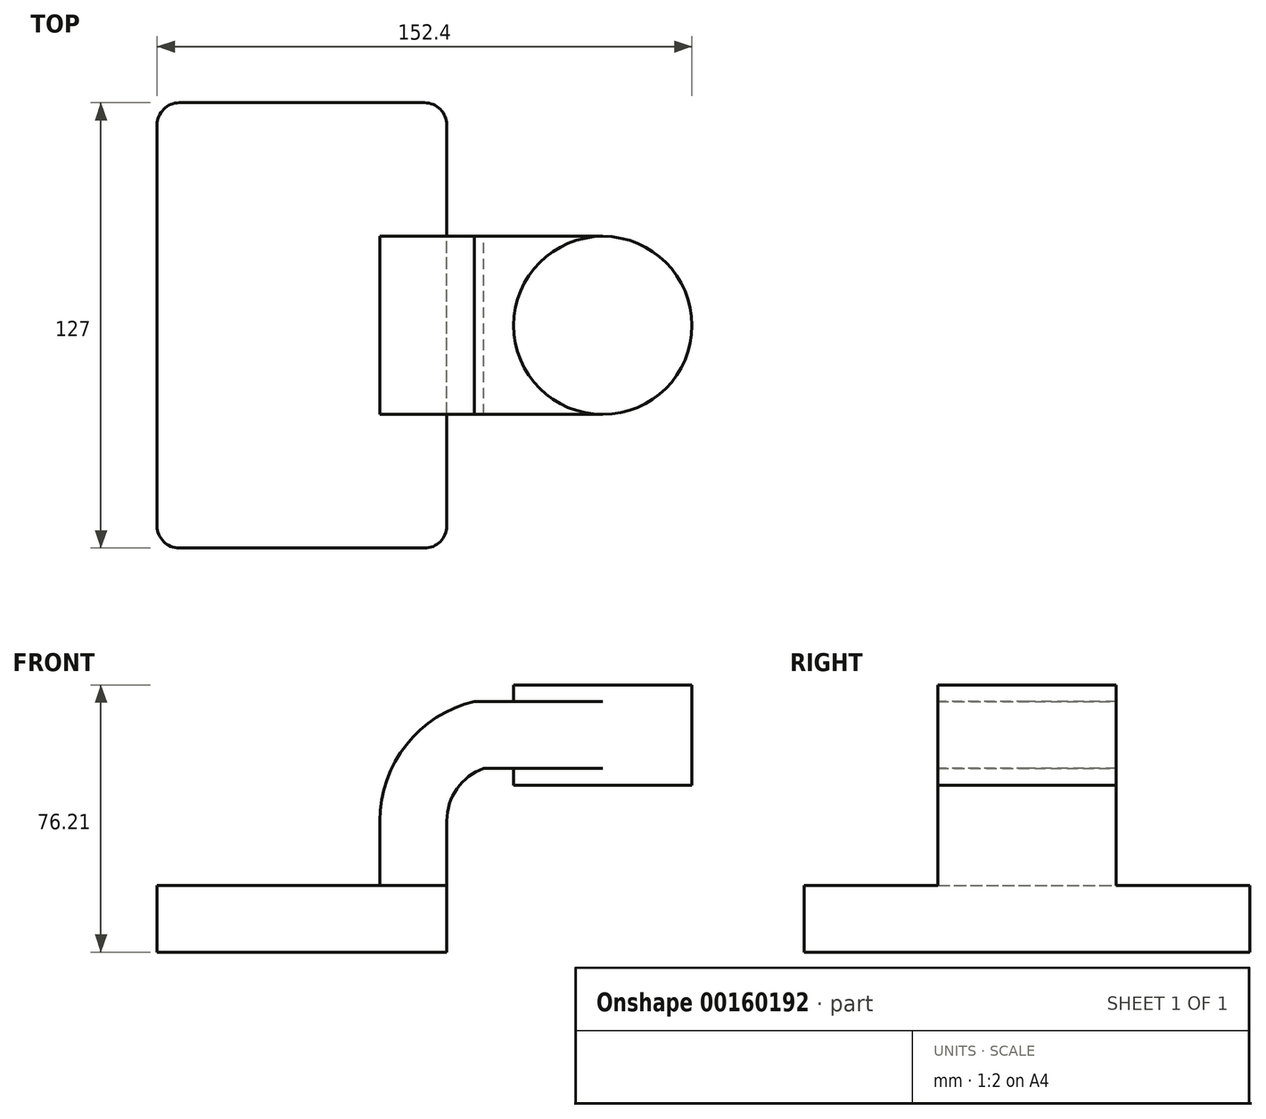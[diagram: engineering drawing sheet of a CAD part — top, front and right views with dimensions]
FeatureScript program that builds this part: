
annotation { "Feature Type Name" : "Feature", "Feature Type Description" : "" }
export const myFeature = defineFeature(function(context is Context, id is Id, definition is map)
    precondition{}
    {
        {
            var Q0;
            Q0=qCreatedBy(makeId("Front.planeOp"),FACE);
            var sketch = newSketch(context, id + "F0", { "sketchPlane" : qUnion([Q0])});
            skLineSegment(sketch, "E0.bottom", {"start": v(-41.28, 9.52) * mm, "end": v(41.28, 9.53) * mm});
            skLineSegment(sketch, "E0.top", {"start": v(-41.28, -9.53) * mm, "end": v(41.28, -9.53) * mm});
            skLineSegment(sketch, "E0.left", {"start": v(-41.28, 9.52) * mm, "end": v(-41.27, -9.53) * mm});
            skLineSegment(sketch, "E0.right", {"start": v(41.27, 9.53) * mm, "end": v(41.28, -9.52) * mm});
            skPoint(sketch, "E0.middle", {"position": v(0, 0) * mm});
            skLineSegment(sketch, "E1.bottom", {"start": v(111.12, 38.1) * mm, "end": v(60.32, 38.1) * mm});
            skLineSegment(sketch, "E1.top", {"start": v(111.12, 66.68) * mm, "end": v(60.32, 66.68) * mm});
            skLineSegment(sketch, "E1.left", {"start": v(111.12, 38.1) * mm, "end": v(111.12, 66.68) * mm});
            skLineSegment(sketch, "E1.right", {"start": v(60.32, 38.1) * mm, "end": v(60.32, 66.68) * mm});
            skPoint(sketch, "E1.middle", {"position": v(85.72, 52.39) * mm});
            skLineSegment(sketch, "E2", {"start": v(41.27, 9.52) * mm, "end": v(41.27, 27.94) * mm});
            skArc(sketch, "E3", {"start": v(41.28, 27.94) * mm, "mid": v(44.16, 37.07) * mm, "end": v(51.77, 42.88) * mm});
            skLineSegment(sketch, "E4", {"start": v(51.77, 42.88) * mm, "end": v(107.14, 42.88) * mm});
            skLineSegment(sketch, "E5.0", {"start": v(49.1, 61.93) * mm, "end": v(85.72, 61.93) * mm});
            skArc(sketch, "E5.1", {"start": v(22.23, 27.94) * mm, "mid": v(29.76, 49.6) * mm, "end": v(49.1, 61.93) * mm});
            skLineSegment(sketch, "E5.2", {"start": v(22.22, 9.52) * mm, "end": v(22.22, 27.94) * mm});
            skLineSegment(sketch, "E6", {"start": v(85.72, 38.1) * mm, "end": v(85.72, 61.93) * mm});
            skLineSegment(sketch, "E7", {"start": v(85.72, 61.93) * mm, "end": v(85.72, 66.68) * mm});
            skFitSpline(sketch, "E8", {"points": [v(-41.28, 9.52) * mm, v(49.1, 61.93) * mm], "startDerivative": vector(0.43, 78.43) * mm, "endDerivative": vector(112.9, -3.22) * mm});
            skSolve(sketch);
        }
        {
            var Q0;
            Q0=makeQuery(id+"F0.imprint","IMPRINT",FACE,{"disambiguationData":[TD([[makeQuery(id+"F0.imprint","IMPRINT",EDGE,{"derivedFrom":sQuery(id+"F0.wireOp",EDGE,"E0.top")}),1.0]])]});
            extrude(context, id + "F1", {"entities" : qUnion([Q0]), "endBound" : BoundingType.SYMMETRIC, "depth" : 127 * mm});
        }
        {
            var Q0;
            {var subQ1=sQuery(id+"F0.wireOp",EDGE,"E2");Q0=makeQuery(id+"F0.imprint","IMPRINT",FACE,{"disambiguationData":[TD([[makeQuery(id+"F0.imprint","IMPRINT",EDGE,{"derivedFrom":subQ1}),1.0]])]});}
            var Q1;
            {var subQ0=sQuery(id+"F0.wireOp",EDGE,"E4");var subQ1=sQuery(id+"F0.wireOp",EDGE,"E1.right");var subQ2=makeQuery(id+"F0.imprint","INTERSECT",VERTEX,{"derivedFrom":[subQ1,subQ0]});Q1=makeQuery(id+"F0.imprint","IMPRINT",FACE,{"disambiguationData":[TD([[makeQuery(id+"F0.imprint","IMPRINT",EDGE,{"disambiguationData":[TD([[subQ2,-1.0]])],"derivedFrom":subQ1}),-1.0]])]});}
            extrude(context, id + "F2", {"entities" : qUnion([Q0, Q1]), "operationType" : NewBodyOperationType.ADD, "endBound" : BoundingType.SYMMETRIC, "depth" : 50.8 * mm});
        }
        {
            var Q0;
            Q0=makeQuery(id+"F0.imprint","IMPRINT",FACE,{"disambiguationData":[TD([[makeQuery(id+"F0.imprint","IMPRINT",EDGE,{"derivedFrom":sQuery(id+"F0.wireOp",EDGE,"E5.1")}),1.0]])]});
            extrude(context, id + "F3", {"entities" : qUnion([Q0]), "operationType" : NewBodyOperationType.ADD, "endBound" : BoundingType.SYMMETRIC, "depth" : 15.88 * mm});
        }
        {
            var Q0;
            {var subQ0=sQuery(id+"F0.wireOp",EDGE,"E1.left");Q0=makeQuery(id+"F0.imprint","IMPRINT",FACE,{"disambiguationData":[TD([[makeQuery(id+"F0.imprint","IMPRINT",EDGE,{"derivedFrom":subQ0}),1.0]])]});}
            var Q1;
            Q1=sQuery(id+"F0.wireOp",EDGE,"E6");
            revolve(context, id + "F4", {"operationType" : NewBodyOperationType.ADD, "entities" : qUnion([Q0]), "axis" : qUnion([Q1]), "revolveType" : RevolveType.FULL});
        }
        {
            var Q0;
            Q0=makeQuery(id+"F1.opExtrude","CAP_EDGE",EDGE,{"disambiguationData":[OSD([sQuery(id+"F0.wireOp",EDGE,"E0.right")])],"isStart":false});
            var Q1;
            Q1=makeQuery(id+"F1.opExtrude","CAP_EDGE",EDGE,{"disambiguationData":[OSD([sQuery(id+"F0.wireOp",EDGE,"E0.left")])],"isStart":false});
            var Q2;
            Q2=makeQuery(id+"F1.opExtrude","CAP_EDGE",EDGE,{"disambiguationData":[OSD([sQuery(id+"F0.wireOp",EDGE,"E0.right")])],"isStart":true});
            var Q3;
            Q3=makeQuery(id+"F1.opExtrude","CAP_EDGE",EDGE,{"disambiguationData":[OSD([sQuery(id+"F0.wireOp",EDGE,"E0.left")])],"isStart":true});
            fillet(context, id + "F5", {"entities" : qUnion([Q0, Q1, Q2, Q3]), "radius" : 6.35 * mm, "tangentPropagation" : true, "allowEdgeOverflow" : false});
        }
    });
